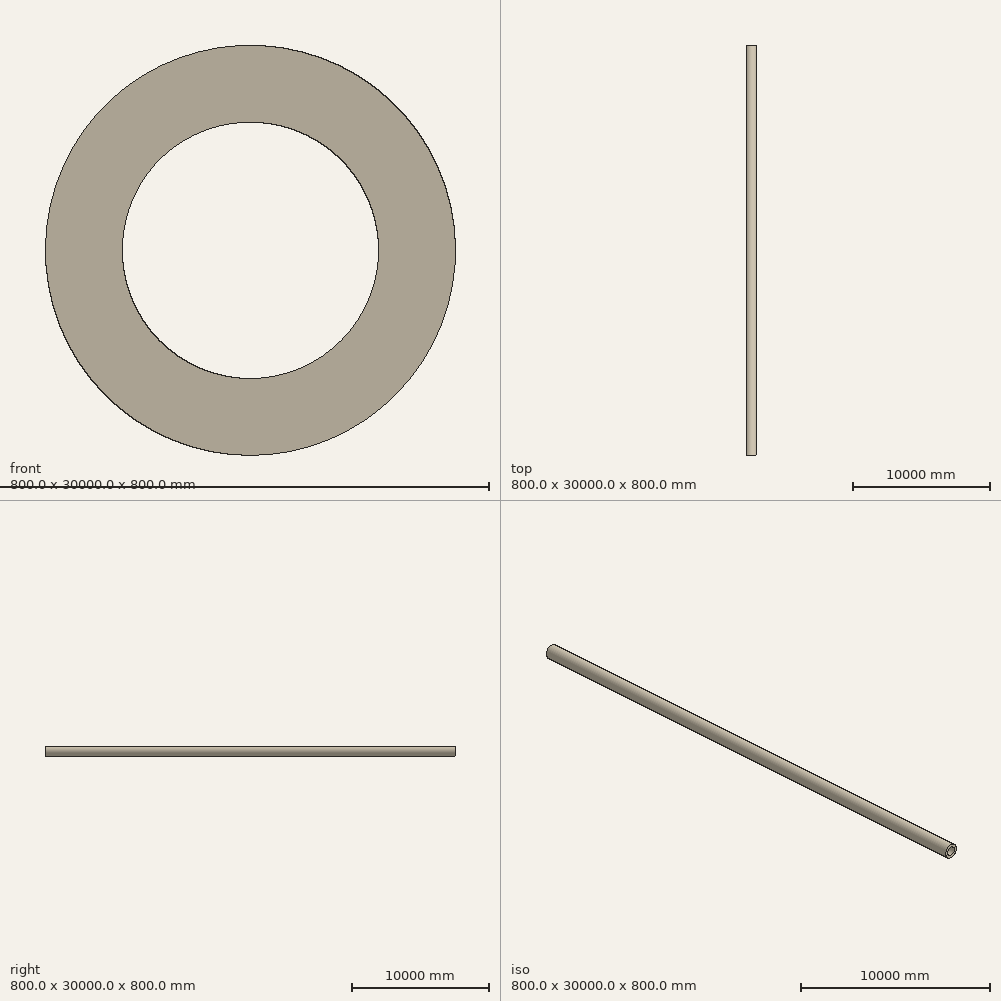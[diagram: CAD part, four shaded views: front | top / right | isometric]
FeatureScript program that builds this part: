
annotation { "Feature Type Name" : "Feature", "Feature Type Description" : "" }
export const myFeature = defineFeature(function(context is Context, id is Id, definition is map)
    precondition{}
    {
        {
            var Q0;
            Q0=qCreatedBy(makeId("Front.planeOp"),FACE);
            var sketch = newSketch(context, id + "F0", { "sketchPlane" : qUnion([Q0])});
            skCircle(sketch, "E0", {"center": v(0, 0) * mm, "radius": 250 * mm});
            skCircle(sketch, "E1.0", {"center": v(0, 0) * mm, "radius": 400 * mm});
            skSolve(sketch);
        }
        {
            var Q0;
            Q0=makeQuery(id+"F0.imprint","IMPRINT",FACE,{"disambiguationData":[TD([[makeQuery(id+"F0.imprint","IMPRINT",EDGE,{"derivedFrom":sQuery(id+"F0.wireOp",EDGE,"E0")}),-1.0]])]});
            extrude(context, id + "F1", {"entities" : qUnion([Q0]), "depth" : 30000 * mm});
        }
    });
